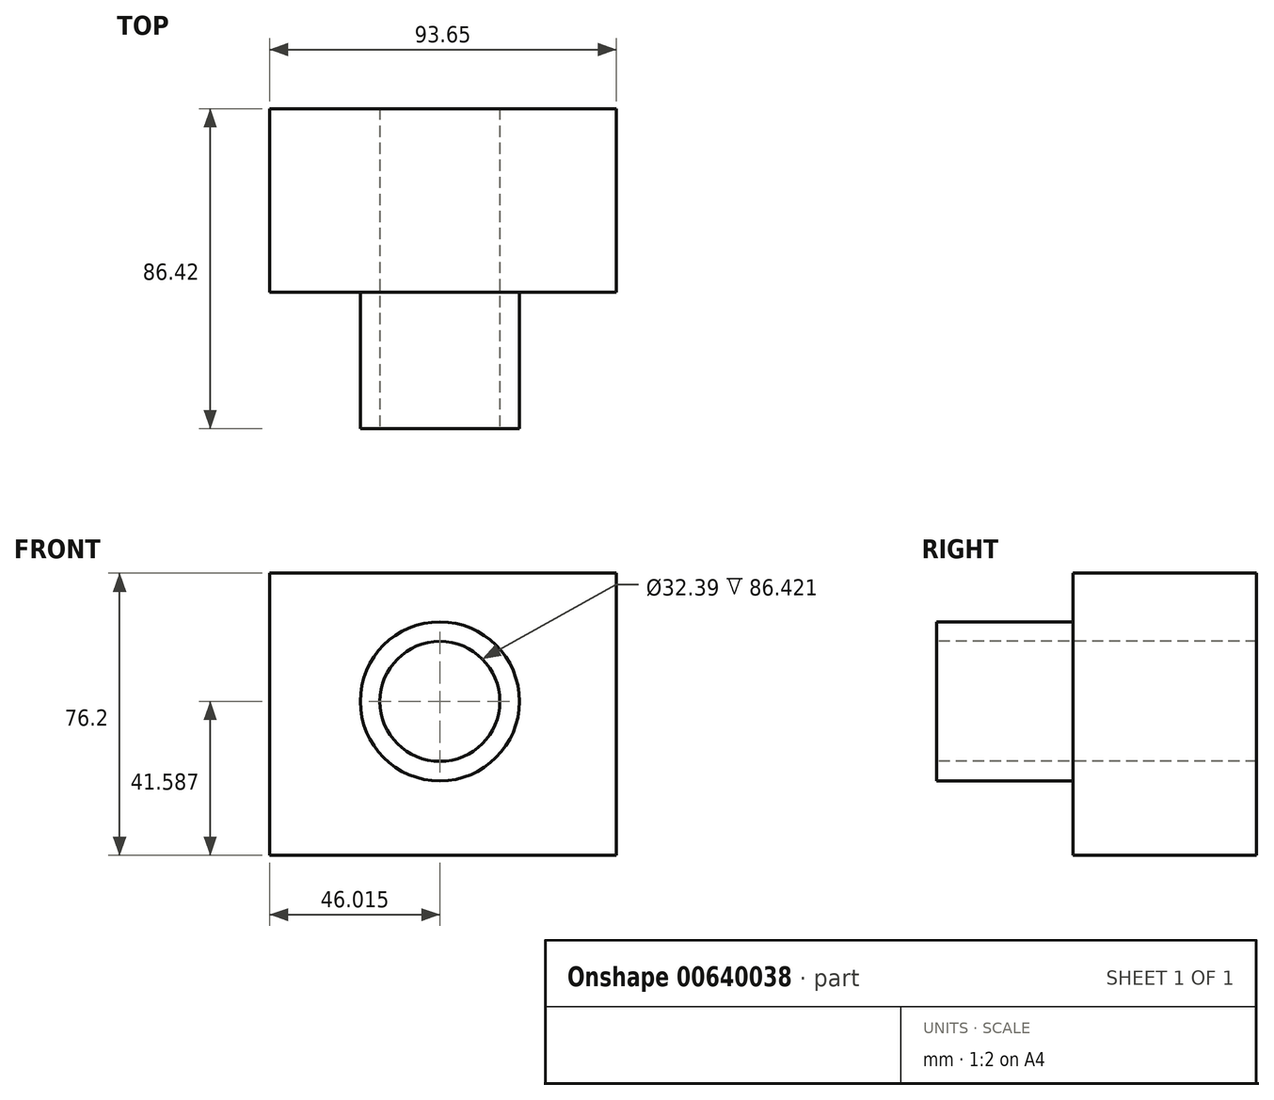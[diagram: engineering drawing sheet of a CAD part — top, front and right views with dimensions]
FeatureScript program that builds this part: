
annotation { "Feature Type Name" : "Feature", "Feature Type Description" : "" }
export const myFeature = defineFeature(function(context is Context, id is Id, definition is map)
    precondition{}
    {
        {
            var Q0;
            Q0=qCreatedBy(makeId("Top.planeOp"),FACE);
            var sketch = newSketch(context, id + "F0", { "sketchPlane" : qUnion([Q0])});
            skLineSegment(sketch, "E0", {"start": v(-48.4, 33.1) * mm, "end": v(-48.4, -16.5) * mm});
            skLineSegment(sketch, "E1", {"start": v(-48.4, -16.5) * mm, "end": v(45.26, -16.5) * mm});
            skLineSegment(sketch, "E2", {"start": v(45.26, -16.5) * mm, "end": v(45.26, 33.1) * mm});
            skLineSegment(sketch, "E3", {"start": v(45.26, 33.1) * mm, "end": v(-48.4, 33.1) * mm});
            skSolve(sketch);
        }
        {
            var Q0;
            Q0=makeQuery(id+"F0.imprint","IMPRINT",FACE,{"disambiguationData":[TD([[makeQuery(id+"F0.imprint","IMPRINT",EDGE,{"derivedFrom":sQuery(id+"F0.wireOp",EDGE,"E0")}),1.0]])]});
            extrude(context, id + "F1", {"entities" : qUnion([Q0]), "depth" : 76.2 * mm, "offsetDistance" : 25.4 * mm});
        }
        {
            var Q0;
            Q0=makeQuery(id+"F1.opExtrude","SWEPT_FACE",FACE,{"disambiguationData":[OSD([sQuery(id+"F0.wireOp",EDGE,"E1")])]});
            var sketch = newSketch(context, id + "F2", { "sketchPlane" : qUnion([Q0])});
            skCircle(sketch, "E4", {"center": v(-2.38, 41.59) * mm, "radius": 16.2 * mm});
            skSolve(sketch);
        }
        {
            var Q0;
            Q0=makeQuery(id+"F2.imprint","IMPRINT",FACE,{"disambiguationData":[TD([[makeQuery(id+"F2.imprint","IMPRINT",EDGE,{"derivedFrom":sQuery(id+"F2.wireOp",EDGE,"E4")}),1.0]])]});
            extrude(context, id + "F3", {"entities" : qUnion([Q0]), "operationType" : NewBodyOperationType.REMOVE, "oppositeDirection" : true, "depth" : 50.8 * mm, "offsetDistance" : 25.4 * mm});
        }
        {
            var Q0;
            Q0=makeQuery(id+"F1.opExtrude","SWEPT_FACE",FACE,{"disambiguationData":[OSD([sQuery(id+"F0.wireOp",EDGE,"E1")])]});
            var sketch = newSketch(context, id + "F4", { "sketchPlane" : qUnion([Q0])});
            skCircle(sketch, "E5", {"center": v(-2.38, 41.59) * mm, "radius": 21.47 * mm});
            skSolve(sketch);
        }
        {
            var Q0;
            Q0=makeQuery(id+"F4.imprint","IMPRINT",FACE,{"disambiguationData":[TD([[makeQuery(id+"F4.imprint","IMPRINT",EDGE,{"derivedFrom":sQuery(id+"F4.wireOp",EDGE,"E5")}),1.0]])]});
            extrude(context, id + "F5", {"entities" : qUnion([Q0]), "operationType" : NewBodyOperationType.ADD, "depth" : 36.83 * mm, "offsetDistance" : 25.4 * mm});
        }
    });
